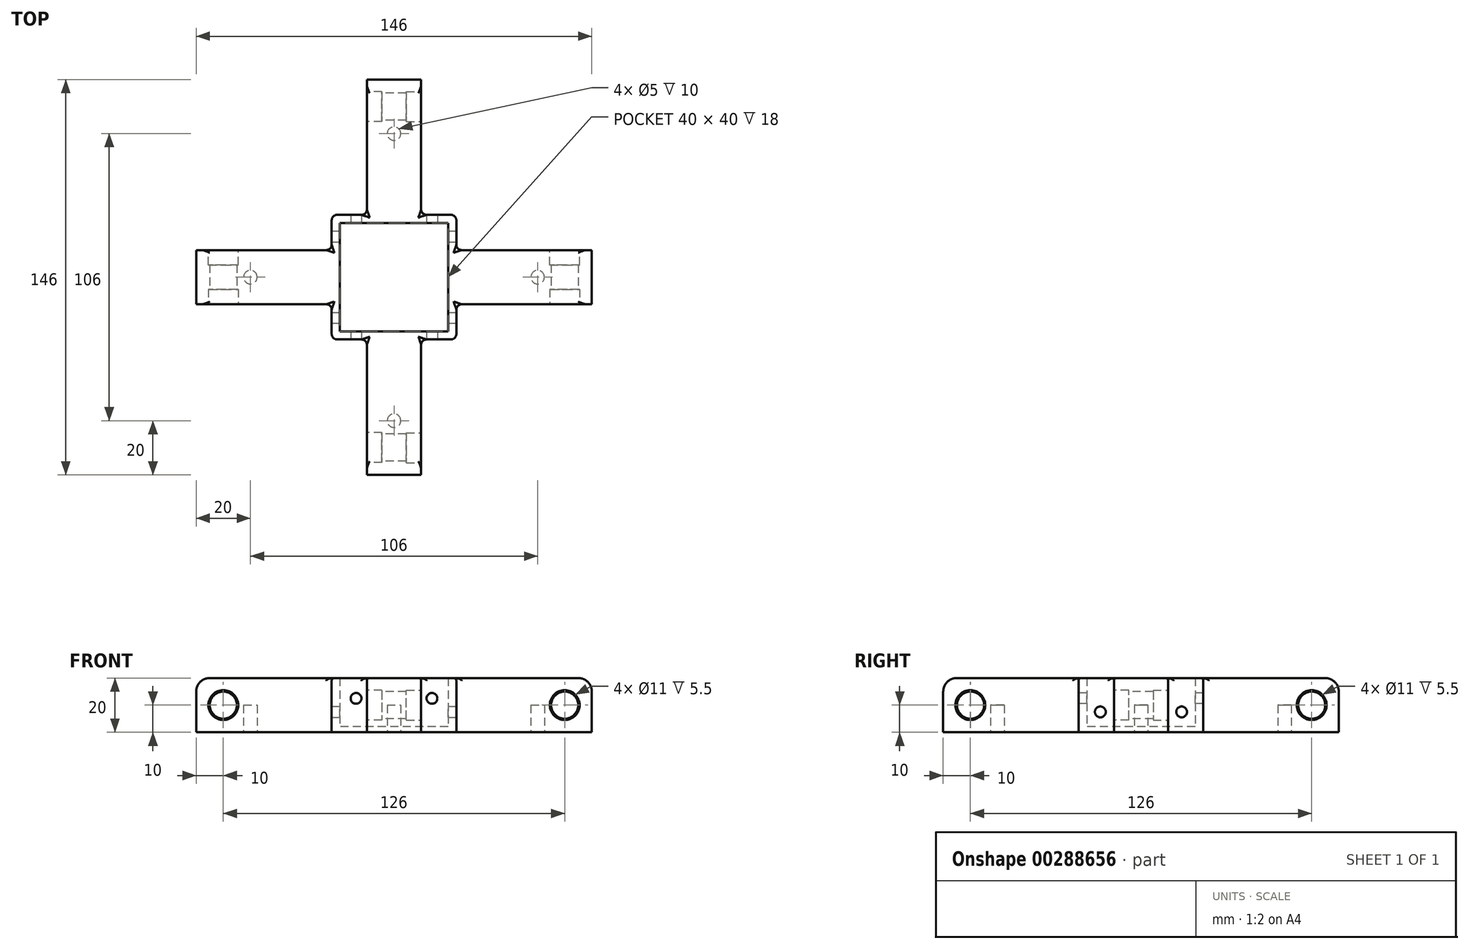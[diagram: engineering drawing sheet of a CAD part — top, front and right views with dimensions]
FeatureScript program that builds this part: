
annotation { "Feature Type Name" : "Feature", "Feature Type Description" : "" }
export const myFeature = defineFeature(function(context is Context, id is Id, definition is map)
    precondition{}
    {
        {
            var Q0;
            Q0=qCreatedBy(makeId("Top.planeOp"),FACE);
            var sketch = newSketch(context, id + "F0", { "sketchPlane" : qUnion([Q0])});
            skPoint(sketch, "E0.middle", {"position": v(0, 0) * mm});
            skLineSegment(sketch, "E1.bottom", {"start": v(20, 20) * mm, "end": v(-20, 20) * mm});
            skLineSegment(sketch, "E1.top", {"start": v(20, -20) * mm, "end": v(-20, -20) * mm});
            skLineSegment(sketch, "E1.left", {"start": v(20, 20) * mm, "end": v(20, -20) * mm});
            skLineSegment(sketch, "E1.right", {"start": v(-20, 20) * mm, "end": v(-20, -20) * mm});
            skLineSegment(sketch, "E2.bottom", {"start": v(-10, 23) * mm, "end": v(10, 23) * mm});
            skLineSegment(sketch, "E2.top", {"start": v(-10, 73) * mm, "end": v(10, 73) * mm});
            skLineSegment(sketch, "E2.left", {"start": v(-10, 23) * mm, "end": v(-10, 73) * mm});
            skLineSegment(sketch, "E2.right", {"start": v(10, 23) * mm, "end": v(10, 73) * mm});
            skLineSegment(sketch, "E3.bottom", {"start": v(23, 10) * mm, "end": v(73, 10) * mm});
            skLineSegment(sketch, "E3.top", {"start": v(23, -10) * mm, "end": v(73, -10) * mm});
            skLineSegment(sketch, "E3.left", {"start": v(23, 10) * mm, "end": v(23, -10) * mm});
            skLineSegment(sketch, "E3.right", {"start": v(73, 10) * mm, "end": v(73, -10) * mm});
            skLineSegment(sketch, "E4.bottom", {"start": v(-23, -10) * mm, "end": v(-73, -10) * mm});
            skLineSegment(sketch, "E4.top", {"start": v(-23, 10) * mm, "end": v(-73, 10) * mm});
            skLineSegment(sketch, "E4.left", {"start": v(-23, -10) * mm, "end": v(-23, 10) * mm});
            skLineSegment(sketch, "E4.right", {"start": v(-73, -10) * mm, "end": v(-73, 10) * mm});
            skLineSegment(sketch, "E5.bottom", {"start": v(23, 23) * mm, "end": v(-23, 23) * mm});
            skLineSegment(sketch, "E5.left", {"start": v(23, 23) * mm, "end": v(23, -23) * mm});
            skLineSegment(sketch, "E5.right", {"start": v(-23, 23) * mm, "end": v(-23, -23) * mm});
            skLineSegment(sketch, "E6", {"start": v(-10, -23) * mm, "end": v(-10, -73) * mm});
            skLineSegment(sketch, "E7", {"start": v(-10, -73) * mm, "end": v(10, -73) * mm});
            skLineSegment(sketch, "E8", {"start": v(10, -73) * mm, "end": v(10, -23) * mm});
            skLineSegment(sketch, "E9", {"start": v(-23, -23) * mm, "end": v(23, -23) * mm});
            skSolve(sketch);
        }
        {
            var Q0;
            Q0=makeQuery(id+"F0.imprint","IMPRINT",FACE,{"disambiguationData":[TD([[makeQuery(id+"F0.imprint","IMPRINT",EDGE,{"derivedFrom":sQuery(id+"F0.wireOp",EDGE,"E2.top")}),-1.0]])]});
            var Q1;
            {var subQ0=sQuery(id+"F0.wireOp",EDGE,"E4.bottom");Q1=makeQuery(id+"F0.imprint","IMPRINT",FACE,{"disambiguationData":[TD([[makeQuery(id+"F0.imprint","IMPRINT",EDGE,{"derivedFrom":subQ0}),-1.0]])]});}
            var Q2;
            {var subQ0=sQuery(id+"F0.wireOp",EDGE,"E6");Q2=makeQuery(id+"F0.imprint","IMPRINT",FACE,{"disambiguationData":[TD([[makeQuery(id+"F0.imprint","IMPRINT",EDGE,{"derivedFrom":subQ0}),1.0]])]});}
            var Q3;
            {var subQ0=sQuery(id+"F0.wireOp",EDGE,"E3.bottom");Q3=makeQuery(id+"F0.imprint","IMPRINT",FACE,{"disambiguationData":[TD([[makeQuery(id+"F0.imprint","IMPRINT",EDGE,{"derivedFrom":subQ0}),-1.0]])]});}
            var Q4;
            Q4=makeQuery(id+"F0.imprint","IMPRINT",FACE,{"disambiguationData":[TD([[makeQuery(id+"F0.imprint","IMPRINT",EDGE,{"derivedFrom":sQuery(id+"F0.wireOp",EDGE,"E1.bottom")}),-1.0]])]});
            extrude(context, id + "F1", {"entities" : qUnion([Q0, Q1, Q2, Q3, Q4]), "depth" : 18 * mm});
        }
        {
            var Q0;
            Q0=makeQuery(id+"F1.opExtrude","SWEPT_FACE",FACE,{"disambiguationData":[OSD([sQuery(id+"F0.wireOp",EDGE,"E4.bottom")])]});
            var sketch = newSketch(context, id + "F2", { "sketchPlane" : qUnion([Q0])});
            skCircle(sketch, "E10", {"center": v(63, 8) * mm, "radius": 5.5 * mm});
            skCircle(sketch, "E11", {"center": v(-63, 8) * mm, "radius": 5.5 * mm});
            skSolve(sketch);
        }
        {
            var Q0;
            Q0=makeQuery(id+"F2.imprint","IMPRINT",FACE,{"disambiguationData":[TD([[makeQuery(id+"F2.imprint","IMPRINT",EDGE,{"derivedFrom":sQuery(id+"F2.wireOp",EDGE,"E11")}),1.0]])]});
            var Q1;
            Q1=makeQuery(id+"F2.imprint","IMPRINT",FACE,{"disambiguationData":[TD([[makeQuery(id+"F2.imprint","IMPRINT",EDGE,{"derivedFrom":sQuery(id+"F2.wireOp",EDGE,"E10")}),1.0]])]});
            extrude(context, id + "F3", {"entities" : qUnion([Q0, Q1]), "operationType" : NewBodyOperationType.REMOVE, "oppositeDirection" : true, "depth" : 5.5 * mm, "offsetDistance" : 25 * mm});
        }
        {
            var Q0;
            Q0=makeQuery(id+"F1.opExtrude","SWEPT_FACE",FACE,{"disambiguationData":[OSD([sQuery(id+"F0.wireOp",EDGE,"E2.right")])]});
            var sketch = newSketch(context, id + "F4", { "sketchPlane" : qUnion([Q0])});
            skCircle(sketch, "E12", {"center": v(-63, 8) * mm, "radius": 5.5 * mm});
            skCircle(sketch, "E13", {"center": v(63, 8) * mm, "radius": 5.5 * mm});
            skSolve(sketch);
        }
        {
            var Q0;
            Q0=makeQuery(id+"F4.imprint","IMPRINT",FACE,{"disambiguationData":[TD([[makeQuery(id+"F4.imprint","IMPRINT",EDGE,{"derivedFrom":sQuery(id+"F4.wireOp",EDGE,"E12")}),1.0]])]});
            var Q1;
            Q1=makeQuery(id+"F4.imprint","IMPRINT",FACE,{"disambiguationData":[TD([[makeQuery(id+"F4.imprint","IMPRINT",EDGE,{"derivedFrom":sQuery(id+"F4.wireOp",EDGE,"E13")}),1.0]])]});
            extrude(context, id + "F5", {"entities" : qUnion([Q0, Q1]), "operationType" : NewBodyOperationType.REMOVE, "oppositeDirection" : true, "depth" : 5.5 * mm, "offsetDistance" : 25 * mm});
        }
        {
            var Q0;
            Q0=makeQuery(id+"F1.opExtrude","CAP_FACE",FACE,{"disambiguationData":[OSD([sQuery(id+"F0.wireOp",EDGE,"E0.bottom"),sQuery(id+"F0.wireOp",EDGE,"E0.top"),sQuery(id+"F0.wireOp",EDGE,"E0.left"),sQuery(id+"F0.wireOp",EDGE,"E0.right"),sQuery(id+"F0.wireOp",EDGE,"E1.bottom"),sQuery(id+"F0.wireOp",EDGE,"E1.top"),sQuery(id+"F0.wireOp",EDGE,"E1.left"),sQuery(id+"F0.wireOp",EDGE,"E1.right"),sQuery(id+"F0.wireOp",EDGE,"E2.top"),sQuery(id+"F0.wireOp",EDGE,"E2.left"),sQuery(id+"F0.wireOp",EDGE,"E2.right"),sQuery(id+"F0.wireOp",EDGE,"E3.bottom"),sQuery(id+"F0.wireOp",EDGE,"E3.top"),sQuery(id+"F0.wireOp",EDGE,"E3.right"),sQuery(id+"F0.wireOp",EDGE,"e9ed0a2b-adfa-4ff0-8274-8b2c5a844dc5.top"),sQuery(id+"F0.wireOp",EDGE,"e9ed0a2b-adfa-4ff0-8274-8b2c5a844dc5.left"),sQuery(id+"F0.wireOp",EDGE,"e9ed0a2b-adfa-4ff0-8274-8b2c5a844dc5.right"),sQuery(id+"F0.wireOp",EDGE,"E4.bottom"),sQuery(id+"F0.wireOp",EDGE,"E4.top"),sQuery(id+"F0.wireOp",EDGE,"E4.right"),sQuery(id+"F0.wireOp",EDGE,"cb328929-7a74-47ee-bcaa-33ff47963f88"),sQuery(id+"F0.wireOp",EDGE,"44ee5794-cfb0-4235-9222-48f7e0f75c5b"),sQuery(id+"F0.wireOp",EDGE,"efc640e9-e7f5-4566-91af-7cc015cf4d55"),sQuery(id+"F0.wireOp",EDGE,"qUu3Md7m-htWJ-nJ3k-l391-mGApce1KwnIF"),sQuery(id+"F0.wireOp",EDGE,"THlYANC8-ntvy-O1bT-XW2g-EfoDZSfK8Oqs"),sQuery(id+"F0.wireOp",EDGE,"KOJT8ZgV-esgi-Uo4k-FNvU-D7jdeVKwvcq7")])],"isStart":true});
            var sketch = newSketch(context, id + "F6", { "sketchPlane" : qUnion([Q0])});
            skLineSegment(sketch, "E14.bottom", {"start": v(-20, 20) * mm, "end": v(20, 20) * mm});
            skLineSegment(sketch, "E14.top", {"start": v(-20, -20) * mm, "end": v(20, -20) * mm});
            skLineSegment(sketch, "E14.left", {"start": v(-20, 20) * mm, "end": v(-20, -20) * mm});
            skLineSegment(sketch, "E14.right", {"start": v(20, 20) * mm, "end": v(20, -20) * mm});
            skSolve(sketch);
        }
        {
            var Q0;
            Q0=makeQuery(id+"F6.imprint","IMPRINT",FACE,{"disambiguationData":[TD([[makeQuery(id+"F6.imprint","IMPRINT",EDGE,{"derivedFrom":sQuery(id+"F6.wireOp",EDGE,"E14.bottom")}),1.0]])]});
            var Q1;
            Q1=makeQuery(id+"F6.imprint","IMPRINT",FACE,{"disambiguationData":[TD([[makeQuery(id+"F6.imprint","IMPRINT",EDGE,{"derivedFrom":sQuery(id+"F6.wireOp",EDGE,"E14.bottom")}),-1.0]])]});
            extrude(context, id + "F7", {"entities" : qUnion([Q0, Q1]), "operationType" : NewBodyOperationType.ADD, "depth" : 2 * mm});
        }
        {
            var Q0;
            {var subQ0=sQuery(id+"F0.wireOp",EDGE,"E6");Q0=makeQuery(id+"F7.boolean.opBoolean","MERGE",FACE,{"derivedFrom":[makeQuery(id+"F1.opExtrude","SWEPT_FACE",FACE,{"disambiguationData":[OSD([subQ0])]}),makeQuery(id+"F7.opExtrude","SWEPT_FACE",FACE,{"disambiguationData":[OSD([subQ0])]})]});}
            var sketch = newSketch(context, id + "F8", { "sketchPlane" : qUnion([Q0])});
            skCircle(sketch, "E15", {"center": v(62.9, 8) * mm, "radius": 5.5 * mm});
            skCircle(sketch, "E16", {"center": v(-63, 8) * mm, "radius": 5.5 * mm});
            skSolve(sketch);
        }
        {
            var Q0;
            Q0=makeQuery(id+"F8.imprint","IMPRINT",FACE,{"disambiguationData":[TD([[makeQuery(id+"F8.imprint","IMPRINT",EDGE,{"derivedFrom":sQuery(id+"F8.wireOp",EDGE,"E16")}),1.0]])]});
            var Q1;
            Q1=makeQuery(id+"F8.imprint","IMPRINT",FACE,{"disambiguationData":[TD([[makeQuery(id+"F8.imprint","IMPRINT",EDGE,{"derivedFrom":sQuery(id+"F8.wireOp",EDGE,"E15")}),1.0]])]});
            extrude(context, id + "F9", {"entities" : qUnion([Q0, Q1]), "operationType" : NewBodyOperationType.REMOVE, "oppositeDirection" : true, "depth" : 5.5 * mm});
        }
        {
            var Q0;
            Q0=makeQuery(id+"F9.boolean.opBoolean","COPY",FACE,{"derivedFrom":makeQuery(id+"F9.opExtrude","CAP_FACE",FACE,{"disambiguationData":[OSD([sQuery(id+"F8.wireOp",EDGE,"E16")])],"isStart":false})});
            var sketch = newSketch(context, id + "F10", { "sketchPlane" : qUnion([Q0])});
            skCircle(sketch, "E17", {"center": v(-63, 8) * mm, "radius": 5 * mm});
            skCircle(sketch, "E18", {"center": v(62.9, 8) * mm, "radius": 5 * mm});
            skSolve(sketch);
        }
        {
            var Q0;
            Q0 = qSketchRegion(id + "F10", true);
            extrude(context, id + "F11", {"entities" : qUnion([Q0]), "operationType" : NewBodyOperationType.REMOVE, "oppositeDirection" : true, "depth" : 10 * mm});
        }
        {
            var Q0;
            Q0=makeQuery(id+"F3.boolean.opBoolean","COPY",FACE,{"derivedFrom":makeQuery(id+"F3.opExtrude","CAP_FACE",FACE,{"disambiguationData":[OSD([sQuery(id+"F2.wireOp",EDGE,"E11")])],"isStart":false})});
            var sketch = newSketch(context, id + "F12", { "sketchPlane" : qUnion([Q0])});
            skCircle(sketch, "E19", {"center": v(-63, 8) * mm, "radius": 5 * mm});
            skCircle(sketch, "E20", {"center": v(63, 8) * mm, "radius": 5 * mm});
            skSolve(sketch);
        }
        {
            var Q0;
            Q0=makeQuery(id+"F12.imprint","IMPRINT",FACE,{"disambiguationData":[TD([[makeQuery(id+"F12.imprint","IMPRINT",EDGE,{"derivedFrom":sQuery(id+"F12.wireOp",EDGE,"E20")}),1.0]])]});
            var Q1;
            Q1=makeQuery(id+"F12.imprint","IMPRINT",FACE,{"disambiguationData":[TD([[makeQuery(id+"F12.imprint","IMPRINT",EDGE,{"derivedFrom":sQuery(id+"F12.wireOp",EDGE,"E19")}),1.0]])]});
            extrude(context, id + "F13", {"entities" : qUnion([Q0, Q1]), "operationType" : NewBodyOperationType.REMOVE, "oppositeDirection" : true, "depth" : 10 * mm});
        }
        {
            var Q0;
            {var subQ0=sQuery(id+"F0.wireOp",EDGE,"E3.bottom");Q0=makeQuery(id+"F7.boolean.opBoolean","MERGE",FACE,{"derivedFrom":[makeQuery(id+"F1.opExtrude","SWEPT_FACE",FACE,{"disambiguationData":[OSD([subQ0])]}),makeQuery(id+"F7.opExtrude","SWEPT_FACE",FACE,{"disambiguationData":[OSD([subQ0])]})]});}
            var sketch = newSketch(context, id + "F14", { "sketchPlane" : qUnion([Q0])});
            skCircle(sketch, "E21", {"center": v(-63, 8) * mm, "radius": 5.5 * mm});
            skCircle(sketch, "E22", {"center": v(63, 8) * mm, "radius": 5.5 * mm});
            skSolve(sketch);
        }
        {
            var Q0;
            Q0=makeQuery(id+"F14.imprint","IMPRINT",FACE,{"disambiguationData":[TD([[makeQuery(id+"F14.imprint","IMPRINT",EDGE,{"derivedFrom":sQuery(id+"F14.wireOp",EDGE,"E21")}),1.0]])]});
            var Q1;
            Q1=makeQuery(id+"F14.imprint","IMPRINT",FACE,{"disambiguationData":[TD([[makeQuery(id+"F14.imprint","IMPRINT",EDGE,{"derivedFrom":sQuery(id+"F14.wireOp",EDGE,"E22")}),1.0]])]});
            extrude(context, id + "F15", {"entities" : qUnion([Q0, Q1]), "operationType" : NewBodyOperationType.REMOVE, "oppositeDirection" : true, "depth" : 5.5 * mm});
        }
        {
            var Q0;
            {var subQ0=sQuery(id+"F0.wireOp",EDGE,"E9");var subQ1=makeQuery(id+"F0.imprint","IMPRINT",EDGE,{"disambiguationData":[TD([[makeQuery(id+"F0.imprint","INTERSECT",VERTEX,{"derivedFrom":[sQuery(id+"F0.wireOp",EDGE,"E5.right"),subQ0]}),-1.0]])],"derivedFrom":subQ0});Q0=makeQuery(id+"F7.boolean.opBoolean","MERGE",FACE,{"derivedFrom":[makeQuery(id+"F1.opExtrude","SWEPT_FACE",FACE,{"disambiguationData":[OSD([subQ0]),TDD([subQ1])]}),makeQuery(id+"F7.opExtrude","SWEPT_FACE",FACE,{"disambiguationData":[OSD([subQ0]),TDD([makeQuery(id+"F6.imprint","IMPRINT",EDGE,{"derivedFrom":makeQuery(id+"F1.opExtrude","CAP_EDGE",EDGE,{"disambiguationData":[OSD([subQ0]),TDD([subQ1])],"isStart":true})})])]})]});}
            var sketch = newSketch(context, id + "F16", { "sketchPlane" : qUnion([Q0])});
            skCircle(sketch, "E23", {"center": v(-14, 10.5) * mm, "radius": 2 * mm});
            skCircle(sketch, "E24", {"center": v(14, 10.5) * mm, "radius": 2 * mm});
            skSolve(sketch);
        }
        {
            var Q0;
            Q0=makeQuery(id+"F16.imprint","IMPRINT",FACE,{"disambiguationData":[TD([[makeQuery(id+"F16.imprint","IMPRINT",EDGE,{"derivedFrom":sQuery(id+"F16.wireOp",EDGE,"E23")}),1.0]])]});
            var Q1;
            Q1=makeQuery(id+"F16.imprint","IMPRINT",FACE,{"disambiguationData":[TD([[makeQuery(id+"F16.imprint","IMPRINT",EDGE,{"derivedFrom":sQuery(id+"F16.wireOp",EDGE,"E24")}),1.0]])]});
            extrude(context, id + "F17", {"entities" : qUnion([Q0, Q1]), "operationType" : NewBodyOperationType.REMOVE, "oppositeDirection" : true, "depth" : 46 * mm, "offsetDistance" : 25 * mm});
        }
        {
            var Q0;
            {var subQ0=sQuery(id+"F0.wireOp",EDGE,"E5.left");var subQ1=makeQuery(id+"F0.imprint","IMPRINT",EDGE,{"disambiguationData":[TD([[makeQuery(id+"F0.imprint","INTERSECT",VERTEX,{"derivedFrom":[sQuery(id+"F0.wireOp",EDGE,"E3.top"),subQ0]}),-1.0]])],"derivedFrom":subQ0});Q0=makeQuery(id+"F7.boolean.opBoolean","MERGE",FACE,{"derivedFrom":[makeQuery(id+"F1.opExtrude","SWEPT_FACE",FACE,{"disambiguationData":[OSD([subQ0]),TDD([subQ1])]}),makeQuery(id+"F7.opExtrude","SWEPT_FACE",FACE,{"disambiguationData":[OSD([subQ0]),TDD([makeQuery(id+"F6.imprint","IMPRINT",EDGE,{"derivedFrom":makeQuery(id+"F1.opExtrude","CAP_EDGE",EDGE,{"disambiguationData":[OSD([subQ0]),TDD([subQ1])],"isStart":true})})])]})]});}
            var sketch = newSketch(context, id + "F18", { "sketchPlane" : qUnion([Q0])});
            skCircle(sketch, "E25", {"center": v(-15, 5.5) * mm, "radius": 2 * mm});
            skCircle(sketch, "E26", {"center": v(15, 5.5) * mm, "radius": 2 * mm});
            skSolve(sketch);
        }
        {
            var Q0;
            Q0=makeQuery(id+"F18.imprint","IMPRINT",FACE,{"disambiguationData":[TD([[makeQuery(id+"F18.imprint","IMPRINT",EDGE,{"derivedFrom":sQuery(id+"F18.wireOp",EDGE,"E25")}),1.0]])]});
            var Q1;
            Q1=makeQuery(id+"F18.imprint","IMPRINT",FACE,{"disambiguationData":[TD([[makeQuery(id+"F18.imprint","IMPRINT",EDGE,{"derivedFrom":sQuery(id+"F18.wireOp",EDGE,"E26")}),1.0]])]});
            extrude(context, id + "F19", {"entities" : qUnion([Q0, Q1]), "operationType" : NewBodyOperationType.REMOVE, "oppositeDirection" : true, "depth" : 46 * mm, "offsetDistance" : 25 * mm});
        }
        {
            var Q0;
            Q0=makeQuery(id+"F7.opExtrude","CAP_FACE",FACE,{"disambiguationData":[OSD([sQuery(id+"F0.wireOp",EDGE,"E2.top"),sQuery(id+"F0.wireOp",EDGE,"E2.left"),sQuery(id+"F0.wireOp",EDGE,"E2.right"),sQuery(id+"F0.wireOp",EDGE,"E3.bottom"),sQuery(id+"F0.wireOp",EDGE,"E3.top"),sQuery(id+"F0.wireOp",EDGE,"E3.right"),sQuery(id+"F0.wireOp",EDGE,"E4.bottom"),sQuery(id+"F0.wireOp",EDGE,"E4.top"),sQuery(id+"F0.wireOp",EDGE,"E4.right"),sQuery(id+"F0.wireOp",EDGE,"E5.bottom"),sQuery(id+"F0.wireOp",EDGE,"E5.left"),sQuery(id+"F0.wireOp",EDGE,"E5.right"),sQuery(id+"F0.wireOp",EDGE,"E6"),sQuery(id+"F0.wireOp",EDGE,"E7"),sQuery(id+"F0.wireOp",EDGE,"E8"),sQuery(id+"F0.wireOp",EDGE,"E9")])],"isStart":false});
            var sketch = newSketch(context, id + "F20", { "sketchPlane" : qUnion([Q0])});
            skCircle(sketch, "E27", {"center": v(0, 53) * mm, "radius": 2.5 * mm});
            skCircle(sketch, "E28", {"center": v(53, 0) * mm, "radius": 2.5 * mm});
            skCircle(sketch, "E29", {"center": v(0, -53) * mm, "radius": 2.5 * mm});
            skCircle(sketch, "E30", {"center": v(-53, 0) * mm, "radius": 2.5 * mm});
            skSolve(sketch);
        }
        {
            var Q0;
            Q0=makeQuery(id+"F20.imprint","IMPRINT",FACE,{"disambiguationData":[TD([[makeQuery(id+"F20.imprint","IMPRINT",EDGE,{"derivedFrom":sQuery(id+"F20.wireOp",EDGE,"E27")}),1.0]])]});
            var Q1;
            Q1=makeQuery(id+"F20.imprint","IMPRINT",FACE,{"disambiguationData":[TD([[makeQuery(id+"F20.imprint","IMPRINT",EDGE,{"derivedFrom":sQuery(id+"F20.wireOp",EDGE,"E28")}),1.0]])]});
            var Q2;
            Q2=makeQuery(id+"F20.imprint","IMPRINT",FACE,{"disambiguationData":[TD([[makeQuery(id+"F20.imprint","IMPRINT",EDGE,{"derivedFrom":sQuery(id+"F20.wireOp",EDGE,"E30")}),1.0]])]});
            var Q3;
            Q3=makeQuery(id+"F20.imprint","IMPRINT",FACE,{"disambiguationData":[TD([[makeQuery(id+"F20.imprint","IMPRINT",EDGE,{"derivedFrom":sQuery(id+"F20.wireOp",EDGE,"E29")}),1.0]])]});
            extrude(context, id + "F21", {"entities" : qUnion([Q0, Q1, Q2, Q3]), "operationType" : NewBodyOperationType.REMOVE, "oppositeDirection" : true, "depth" : 10 * mm, "offsetDistance" : 25 * mm});
        }
        {
            var Q0;
            Q0=makeQuery(id+"F1.opExtrude","CAP_EDGE",EDGE,{"disambiguationData":[OSD([sQuery(id+"F0.wireOp",EDGE,"E4.top")])],"isStart":false});
            var Q1;
            Q1=makeQuery(id+"F1.opExtrude","CAP_EDGE",EDGE,{"disambiguationData":[OSD([sQuery(id+"F0.wireOp",EDGE,"E2.left")])],"isStart":false});
            var Q2;
            Q2=makeQuery(id+"F1.opExtrude","CAP_EDGE",EDGE,{"disambiguationData":[OSD([sQuery(id+"F0.wireOp",EDGE,"E2.right")])],"isStart":false});
            var Q3;
            Q3=makeQuery(id+"F1.opExtrude","CAP_EDGE",EDGE,{"disambiguationData":[OSD([sQuery(id+"F0.wireOp",EDGE,"E3.bottom")])],"isStart":false});
            var Q4;
            Q4=makeQuery(id+"F1.opExtrude","CAP_EDGE",EDGE,{"disambiguationData":[OSD([sQuery(id+"F0.wireOp",EDGE,"E3.top")])],"isStart":false});
            var Q5;
            Q5=makeQuery(id+"F1.opExtrude","CAP_EDGE",EDGE,{"disambiguationData":[OSD([sQuery(id+"F0.wireOp",EDGE,"E8")])],"isStart":false});
            var Q6;
            Q6=makeQuery(id+"F1.opExtrude","CAP_EDGE",EDGE,{"disambiguationData":[OSD([sQuery(id+"F0.wireOp",EDGE,"E6")])],"isStart":false});
            var Q7;
            Q7=makeQuery(id+"F1.opExtrude","CAP_EDGE",EDGE,{"disambiguationData":[OSD([sQuery(id+"F0.wireOp",EDGE,"E4.bottom")])],"isStart":false});
            var Q8;
            {var subQ0=sQuery(id+"F0.wireOp",EDGE,"E9");Q8=makeQuery(id+"F1.opExtrude","CAP_EDGE",EDGE,{"disambiguationData":[OSD([subQ0]),TDD([makeQuery(id+"F0.imprint","IMPRINT",EDGE,{"disambiguationData":[TD([[makeQuery(id+"F0.imprint","INTERSECT",VERTEX,{"derivedFrom":[sQuery(id+"F0.wireOp",EDGE,"E5.left"),subQ0]}),1.0]])],"derivedFrom":subQ0})])],"isStart":false});}
            var Q9;
            {var subQ0=sQuery(id+"F0.wireOp",EDGE,"E5.left");Q9=makeQuery(id+"F1.opExtrude","CAP_EDGE",EDGE,{"disambiguationData":[OSD([subQ0]),TDD([makeQuery(id+"F0.imprint","IMPRINT",EDGE,{"disambiguationData":[TD([[makeQuery(id+"F0.imprint","INTERSECT",VERTEX,{"derivedFrom":[sQuery(id+"F0.wireOp",EDGE,"E3.top"),subQ0]}),-1.0]])],"derivedFrom":subQ0})])],"isStart":false});}
            var Q10;
            {var subQ0=sQuery(id+"F0.wireOp",EDGE,"E5.left");Q10=makeQuery(id+"F1.opExtrude","CAP_EDGE",EDGE,{"disambiguationData":[OSD([subQ0]),TDD([makeQuery(id+"F0.imprint","IMPRINT",EDGE,{"disambiguationData":[TD([[makeQuery(id+"F0.imprint","INTERSECT",VERTEX,{"derivedFrom":[sQuery(id+"F0.wireOp",EDGE,"E3.bottom"),subQ0]}),1.0]])],"derivedFrom":subQ0})])],"isStart":false});}
            var Q11;
            {var subQ0=sQuery(id+"F0.wireOp",EDGE,"E5.bottom");Q11=makeQuery(id+"F1.opExtrude","CAP_EDGE",EDGE,{"disambiguationData":[OSD([subQ0]),TDD([makeQuery(id+"F0.imprint","IMPRINT",EDGE,{"disambiguationData":[TD([[makeQuery(id+"F0.imprint","INTERSECT",VERTEX,{"derivedFrom":[sQuery(id+"F0.wireOp",EDGE,"E2.right"),subQ0]}),1.0]])],"derivedFrom":subQ0})])],"isStart":false});}
            var Q12;
            {var subQ0=sQuery(id+"F0.wireOp",EDGE,"E5.bottom");Q12=makeQuery(id+"F1.opExtrude","CAP_EDGE",EDGE,{"disambiguationData":[OSD([subQ0]),TDD([makeQuery(id+"F0.imprint","IMPRINT",EDGE,{"disambiguationData":[TD([[makeQuery(id+"F0.imprint","INTERSECT",VERTEX,{"derivedFrom":[sQuery(id+"F0.wireOp",EDGE,"E2.left"),subQ0]}),-1.0]])],"derivedFrom":subQ0})])],"isStart":false});}
            var Q13;
            {var subQ0=sQuery(id+"F0.wireOp",EDGE,"E5.right");Q13=makeQuery(id+"F1.opExtrude","CAP_EDGE",EDGE,{"disambiguationData":[OSD([subQ0]),TDD([makeQuery(id+"F0.imprint","IMPRINT",EDGE,{"disambiguationData":[TD([[makeQuery(id+"F0.imprint","INTERSECT",VERTEX,{"derivedFrom":[sQuery(id+"F0.wireOp",EDGE,"E4.top"),subQ0]}),1.0]])],"derivedFrom":subQ0})])],"isStart":false});}
            var Q14;
            {var subQ0=sQuery(id+"F0.wireOp",EDGE,"E9");Q14=makeQuery(id+"F1.opExtrude","CAP_EDGE",EDGE,{"disambiguationData":[OSD([subQ0]),TDD([makeQuery(id+"F0.imprint","IMPRINT",EDGE,{"disambiguationData":[TD([[makeQuery(id+"F0.imprint","INTERSECT",VERTEX,{"derivedFrom":[sQuery(id+"F0.wireOp",EDGE,"E5.right"),subQ0]}),-1.0]])],"derivedFrom":subQ0})])],"isStart":false});}
            var Q15;
            {var subQ0=sQuery(id+"F0.wireOp",EDGE,"E5.right");Q15=makeQuery(id+"F1.opExtrude","CAP_EDGE",EDGE,{"disambiguationData":[OSD([subQ0]),TDD([makeQuery(id+"F0.imprint","IMPRINT",EDGE,{"disambiguationData":[TD([[makeQuery(id+"F0.imprint","INTERSECT",VERTEX,{"derivedFrom":[sQuery(id+"F0.wireOp",EDGE,"E4.bottom"),subQ0]}),-1.0]])],"derivedFrom":subQ0})])],"isStart":false});}
            fillet(context, id + "F22", {"entities" : qUnion([Q0, Q1, Q2, Q3, Q4, Q5, Q6, Q7, Q8, Q9, Q10, Q11, Q12, Q13, Q14, Q15]), "radius" : 1 * mm, "tangentPropagation" : true, "allowEdgeOverflow" : false});
        }
        {
            var Q0;
            {var subQ0=sQuery(id+"F0.wireOp",EDGE,"E9");var subQ1=sQuery(id+"F0.wireOp",EDGE,"E8");Q0=makeQuery(id+"F7.boolean.opBoolean","MERGE",EDGE,{"derivedFrom":[makeQuery(id+"F1.opExtrude","SWEPT_EDGE",EDGE,{"disambiguationData":[OSD([subQ1,subQ0])]}),makeQuery(id+"F7.opExtrude","SWEPT_EDGE",EDGE,{"disambiguationData":[OSD([subQ1,subQ0])]})]});}
            var Q1;
            {var subQ0=sQuery(id+"F0.wireOp",EDGE,"E9");var subQ1=sQuery(id+"F0.wireOp",EDGE,"E5.left");Q1=makeQuery(id+"F7.boolean.opBoolean","MERGE",EDGE,{"derivedFrom":[makeQuery(id+"F1.opExtrude","SWEPT_EDGE",EDGE,{"disambiguationData":[OSD([subQ1,subQ0])]}),makeQuery(id+"F7.opExtrude","SWEPT_EDGE",EDGE,{"disambiguationData":[OSD([subQ1,subQ0])]})]});}
            var Q2;
            {var subQ0=sQuery(id+"F0.wireOp",EDGE,"E5.left");var subQ1=sQuery(id+"F0.wireOp",EDGE,"E3.top");Q2=makeQuery(id+"F7.boolean.opBoolean","MERGE",EDGE,{"derivedFrom":[makeQuery(id+"F1.opExtrude","SWEPT_EDGE",EDGE,{"disambiguationData":[OSD([subQ1,subQ0])]}),makeQuery(id+"F7.opExtrude","SWEPT_EDGE",EDGE,{"disambiguationData":[OSD([subQ1,subQ0])]})]});}
            var Q3;
            {var subQ0=sQuery(id+"F0.wireOp",EDGE,"E5.left");var subQ1=sQuery(id+"F0.wireOp",EDGE,"E5.bottom");Q3=makeQuery(id+"F7.boolean.opBoolean","MERGE",EDGE,{"derivedFrom":[makeQuery(id+"F1.opExtrude","SWEPT_EDGE",EDGE,{"disambiguationData":[OSD([subQ1,subQ0])]}),makeQuery(id+"F7.opExtrude","SWEPT_EDGE",EDGE,{"disambiguationData":[OSD([subQ1,subQ0])]})]});}
            var Q4;
            {var subQ0=sQuery(id+"F0.wireOp",EDGE,"E5.left");var subQ1=sQuery(id+"F0.wireOp",EDGE,"E3.bottom");Q4=makeQuery(id+"F7.boolean.opBoolean","MERGE",EDGE,{"derivedFrom":[makeQuery(id+"F1.opExtrude","SWEPT_EDGE",EDGE,{"disambiguationData":[OSD([subQ1,subQ0])]}),makeQuery(id+"F7.opExtrude","SWEPT_EDGE",EDGE,{"disambiguationData":[OSD([subQ1,subQ0])]})]});}
            var Q5;
            {var subQ0=sQuery(id+"F0.wireOp",EDGE,"E5.bottom");var subQ1=sQuery(id+"F0.wireOp",EDGE,"E2.right");Q5=makeQuery(id+"F7.boolean.opBoolean","MERGE",EDGE,{"derivedFrom":[makeQuery(id+"F1.opExtrude","SWEPT_EDGE",EDGE,{"disambiguationData":[OSD([subQ1,subQ0])]}),makeQuery(id+"F7.opExtrude","SWEPT_EDGE",EDGE,{"disambiguationData":[OSD([subQ1,subQ0])]})]});}
            var Q6;
            {var subQ0=sQuery(id+"F0.wireOp",EDGE,"E5.right");var subQ1=sQuery(id+"F0.wireOp",EDGE,"E4.top");Q6=makeQuery(id+"F7.boolean.opBoolean","MERGE",EDGE,{"derivedFrom":[makeQuery(id+"F1.opExtrude","SWEPT_EDGE",EDGE,{"disambiguationData":[OSD([subQ1,subQ0])]}),makeQuery(id+"F7.opExtrude","SWEPT_EDGE",EDGE,{"disambiguationData":[OSD([subQ1,subQ0])]})]});}
            var Q7;
            {var subQ0=sQuery(id+"F0.wireOp",EDGE,"E5.right");var subQ1=sQuery(id+"F0.wireOp",EDGE,"E5.bottom");Q7=makeQuery(id+"F7.boolean.opBoolean","MERGE",EDGE,{"derivedFrom":[makeQuery(id+"F1.opExtrude","SWEPT_EDGE",EDGE,{"disambiguationData":[OSD([subQ1,subQ0])]}),makeQuery(id+"F7.opExtrude","SWEPT_EDGE",EDGE,{"disambiguationData":[OSD([subQ1,subQ0])]})]});}
            var Q8;
            {var subQ0=sQuery(id+"F0.wireOp",EDGE,"E5.bottom");var subQ1=sQuery(id+"F0.wireOp",EDGE,"E2.left");Q8=makeQuery(id+"F7.boolean.opBoolean","MERGE",EDGE,{"derivedFrom":[makeQuery(id+"F1.opExtrude","SWEPT_EDGE",EDGE,{"disambiguationData":[OSD([subQ1,subQ0])]}),makeQuery(id+"F7.opExtrude","SWEPT_EDGE",EDGE,{"disambiguationData":[OSD([subQ1,subQ0])]})]});}
            var Q9;
            {var subQ0=sQuery(id+"F0.wireOp",EDGE,"E9");var subQ1=sQuery(id+"F0.wireOp",EDGE,"E6");Q9=makeQuery(id+"F7.boolean.opBoolean","MERGE",EDGE,{"derivedFrom":[makeQuery(id+"F1.opExtrude","SWEPT_EDGE",EDGE,{"disambiguationData":[OSD([subQ1,subQ0])]}),makeQuery(id+"F7.opExtrude","SWEPT_EDGE",EDGE,{"disambiguationData":[OSD([subQ1,subQ0])]})]});}
            var Q10;
            {var subQ0=sQuery(id+"F0.wireOp",EDGE,"E9");var subQ1=sQuery(id+"F0.wireOp",EDGE,"E5.right");Q10=makeQuery(id+"F7.boolean.opBoolean","MERGE",EDGE,{"derivedFrom":[makeQuery(id+"F1.opExtrude","SWEPT_EDGE",EDGE,{"disambiguationData":[OSD([subQ1,subQ0])]}),makeQuery(id+"F7.opExtrude","SWEPT_EDGE",EDGE,{"disambiguationData":[OSD([subQ1,subQ0])]})]});}
            var Q11;
            {var subQ0=sQuery(id+"F0.wireOp",EDGE,"E5.right");var subQ1=sQuery(id+"F0.wireOp",EDGE,"E4.bottom");Q11=makeQuery(id+"F7.boolean.opBoolean","MERGE",EDGE,{"derivedFrom":[makeQuery(id+"F1.opExtrude","SWEPT_EDGE",EDGE,{"disambiguationData":[OSD([subQ1,subQ0])]}),makeQuery(id+"F7.opExtrude","SWEPT_EDGE",EDGE,{"disambiguationData":[OSD([subQ1,subQ0])]})]});}
            fillet(context, id + "F23", {"entities" : qUnion([Q0, Q1, Q2, Q3, Q4, Q5, Q6, Q7, Q8, Q9, Q10, Q11]), "radius" : 2 * mm, "tangentPropagation" : true, "allowEdgeOverflow" : false});
        }
        {
            var Q0;
            Q0=makeQuery(id+"F1.opExtrude","CAP_EDGE",EDGE,{"disambiguationData":[OSD([sQuery(id+"F0.wireOp",EDGE,"E4.right")])],"isStart":false});
            var Q1;
            Q1=makeQuery(id+"F1.opExtrude","CAP_EDGE",EDGE,{"disambiguationData":[OSD([sQuery(id+"F0.wireOp",EDGE,"E3.right")])],"isStart":false});
            var Q2;
            Q2=makeQuery(id+"F1.opExtrude","CAP_EDGE",EDGE,{"disambiguationData":[OSD([sQuery(id+"F0.wireOp",EDGE,"E2.top")])],"isStart":false});
            var Q3;
            Q3=makeQuery(id+"F1.opExtrude","CAP_EDGE",EDGE,{"disambiguationData":[OSD([sQuery(id+"F0.wireOp",EDGE,"E7")])],"isStart":false});
            fillet(context, id + "F24", {"entities" : qUnion([Q0, Q1, Q2, Q3]), "radius" : 5 * mm, "allowEdgeOverflow" : false});
        }
    });
